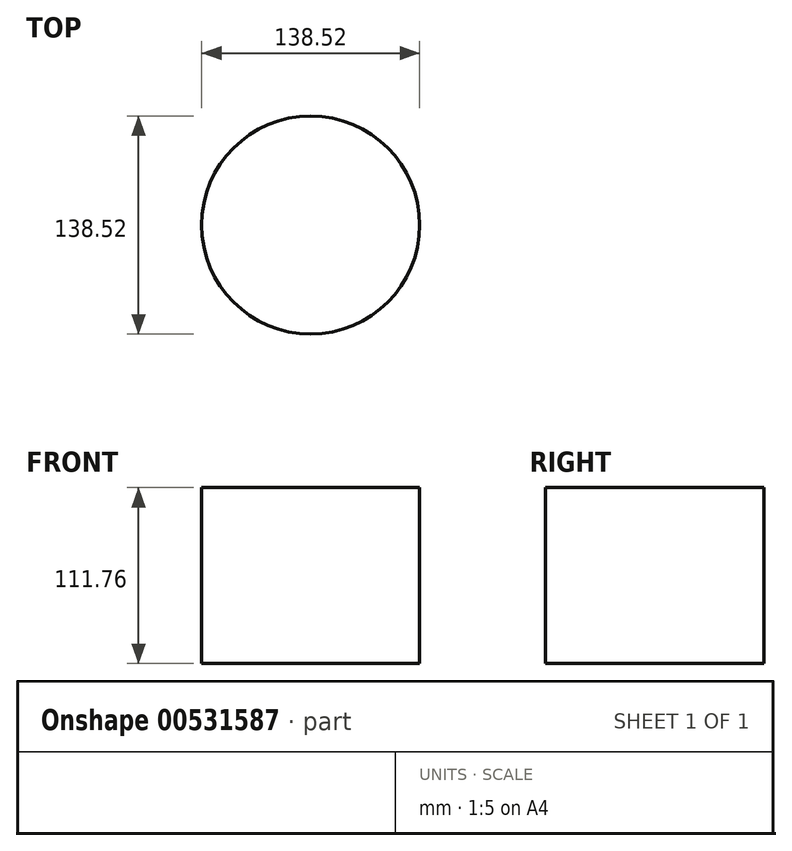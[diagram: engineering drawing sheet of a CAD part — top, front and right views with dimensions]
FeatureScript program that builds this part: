
annotation { "Feature Type Name" : "Feature", "Feature Type Description" : "" }
export const myFeature = defineFeature(function(context is Context, id is Id, definition is map)
    precondition{}
    {
        {
            var Q0;
            Q0=qCreatedBy(makeId("Top.planeOp"),FACE);
            var sketch = newSketch(context, id + "F0", { "sketchPlane" : qUnion([Q0])});
            skCircle(sketch, "E0", {"center": v(0, 0) * mm, "radius": 69.26 * mm});
            skSolve(sketch);
        }
        {
            var Q0;
            Q0 = qSketchRegion(id + "F0", true);
            extrude(context, id + "F1", {"entities" : qUnion([Q0]), "depth" : 111.76 * mm, "offsetDistance" : 25.4 * mm});
        }
    });
